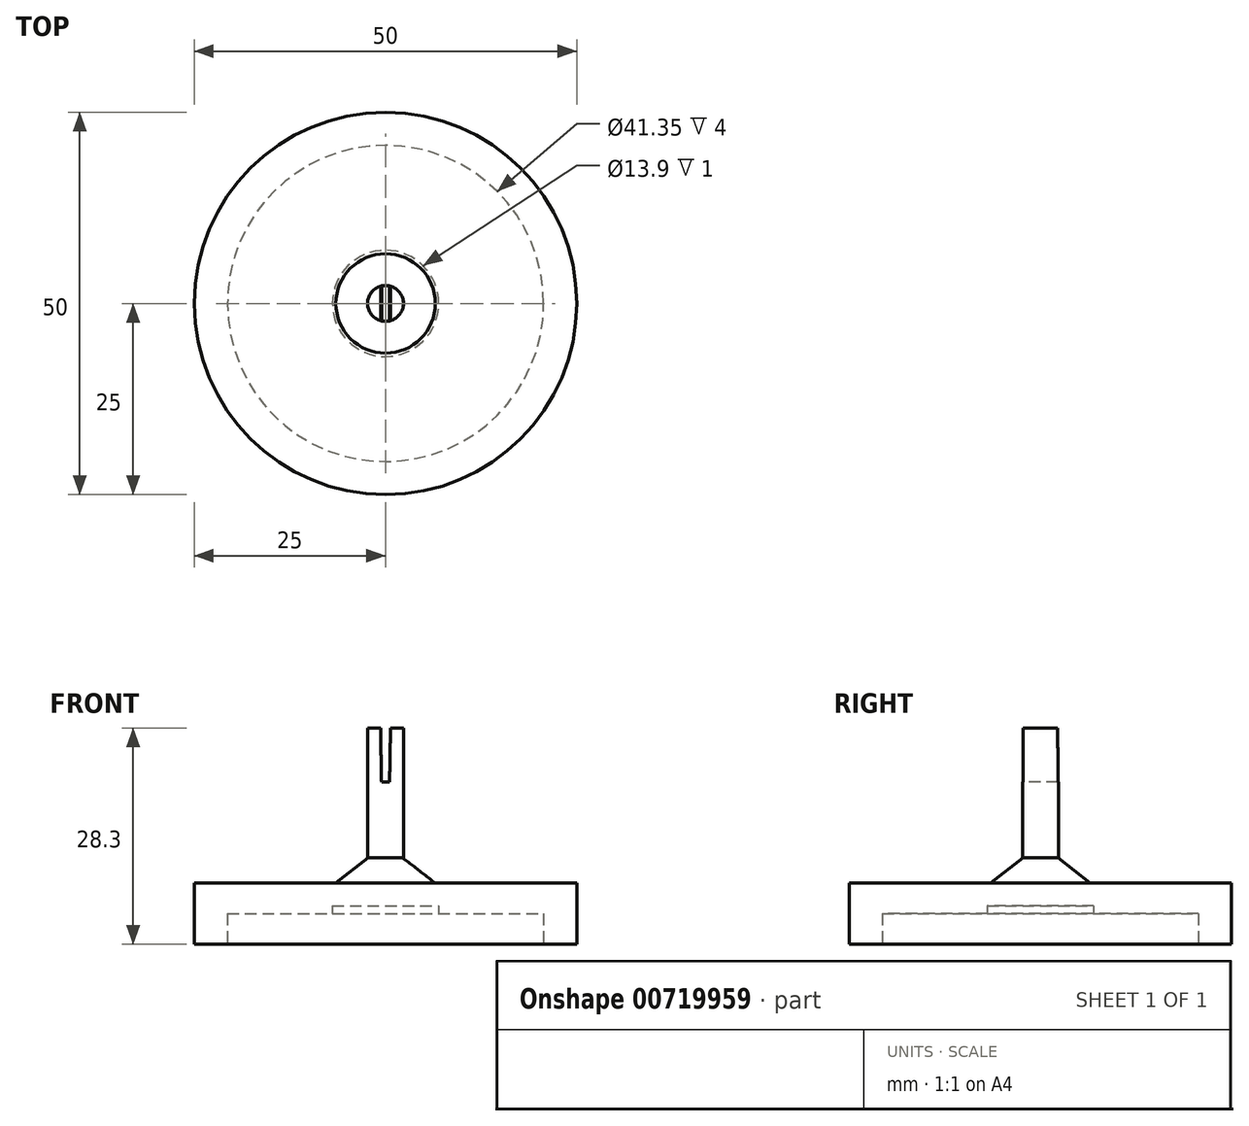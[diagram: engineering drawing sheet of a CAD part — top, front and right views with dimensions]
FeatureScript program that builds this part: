
annotation { "Feature Type Name" : "Feature", "Feature Type Description" : "" }
export const myFeature = defineFeature(function(context is Context, id is Id, definition is map)
    precondition{}
    {
        {
            var Q0;
            Q0=qCreatedBy(makeId("Top.planeOp"),FACE);
            var sketch = newSketch(context, id + "F0", { "sketchPlane" : qUnion([Q0])});
            skCircle(sketch, "E0", {"center": v(0, 0) * mm, "radius": 25 * mm});
            skSolve(sketch);
        }
        {
            var Q0;
            Q0 = qSketchRegion(id + "F0", true);
            extrude(context, id + "F1", {"entities" : qUnion([Q0]), "depth" : 8 * mm, "offsetDistance" : 25 * mm});
        }
        {
            var Q0;
            Q0=makeQuery(id+"F1.opExtrude","CAP_FACE",FACE,{"disambiguationData":[OSD([sQuery(id+"F0.wireOp",EDGE,"E0")])],"isStart":true});
            var sketch = newSketch(context, id + "F2", { "sketchPlane" : qUnion([Q0])});
            skCircle(sketch, "E1", {"center": v(0, 0) * mm, "radius": 20.68 * mm});
            skSolve(sketch);
        }
        {
            var Q0;
            Q0=makeQuery(id+"F2.imprint","IMPRINT",FACE,{"disambiguationData":[TD([[makeQuery(id+"F2.imprint","IMPRINT",EDGE,{"derivedFrom":sQuery(id+"F2.wireOp",EDGE,"E1")}),1.0]])]});
            extrude(context, id + "F3", {"entities" : qUnion([Q0]), "operationType" : NewBodyOperationType.REMOVE, "oppositeDirection" : true, "depth" : 4 * mm, "offsetDistance" : 25 * mm});
        }
        {
            var Q0;
            Q0=makeQuery(id+"F3.boolean.opBoolean","COPY",FACE,{"derivedFrom":makeQuery(id+"F3.opExtrude","CAP_FACE",FACE,{"disambiguationData":[OSD([sQuery(id+"F2.wireOp",EDGE,"E1")])],"isStart":false})});
            var sketch = newSketch(context, id + "F4", { "sketchPlane" : qUnion([Q0])});
            skCircle(sketch, "E2", {"center": v(0, 0) * mm, "radius": 6.95 * mm});
            skSolve(sketch);
        }
        {
            var Q0;
            Q0 = qSketchRegion(id + "F4", true);
            extrude(context, id + "F5", {"entities" : qUnion([Q0]), "operationType" : NewBodyOperationType.REMOVE, "oppositeDirection" : true, "depth" : 1 * mm, "offsetDistance" : 25 * mm});
        }
        {
            var Q0;
            Q0=makeQuery(id+"F1.opExtrude","CAP_FACE",FACE,{"disambiguationData":[OSD([sQuery(id+"F0.wireOp",EDGE,"E0")])],"isStart":false});
            var sketch = newSketch(context, id + "F6", { "sketchPlane" : qUnion([Q0])});
            skCircle(sketch, "E3", {"center": v(0, 0) * mm, "radius": 6.5 * mm});
            skSolve(sketch);
        }
        {
            var Q0;
            Q0=makeQuery(id+"F6.imprint","IMPRINT",FACE,{"disambiguationData":[TD([[makeQuery(id+"F6.imprint","IMPRINT",EDGE,{"derivedFrom":sQuery(id+"F6.wireOp",EDGE,"E3")}),1.0]])]});
            var Q1;
            Q1 = qSketchRegion(id + "F12", true);
            extrude(context, id + "F7", {"entities" : qUnion([Q0, Q1]), "operationType" : NewBodyOperationType.ADD, "depth" : 3.3 * mm, "offsetDistance" : 25 * mm, "hasDraft" : true, "draftAngle" : 52 * degree, "draftPullDirection" : true});
        }
        {
            var Q0;
            Q0=makeQuery(id+"F7.opExtrude","CAP_FACE",FACE,{"disambiguationData":[OSD([sQuery(id+"F6.wireOp",EDGE,"E3")])],"isStart":false});
            var sketch = newSketch(context, id + "F8", { "sketchPlane" : qUnion([Q0])});
            skCircle(sketch, "E4", {"center": v(0, 0) * mm, "radius": 2.35 * mm});
            skSolve(sketch);
        }
        {
            var Q0;
            Q0 = qSketchRegion(id + "F8", true);
            extrude(context, id + "F9", {"entities" : qUnion([Q0]), "operationType" : NewBodyOperationType.ADD, "depth" : 17 * mm, "offsetDistance" : 25 * mm});
        }
        {
            var Q0;
            Q0=makeQuery(id+"F9.opExtrude","CAP_FACE",FACE,{"disambiguationData":[OSD([sQuery(id+"F8.wireOp",EDGE,"E4")])],"isStart":false});
            var sketch = newSketch(context, id + "F10", { "sketchPlane" : qUnion([Q0])});
            skLineSegment(sketch, "E5.bottom", {"start": v(0.65, -4) * mm, "end": v(-0.65, -4) * mm});
            skLineSegment(sketch, "E5.top", {"start": v(0.65, 4) * mm, "end": v(-0.65, 4) * mm});
            skLineSegment(sketch, "E5.left", {"start": v(0.65, -4) * mm, "end": v(0.65, 4) * mm});
            skLineSegment(sketch, "E5.right", {"start": v(-0.65, -4) * mm, "end": v(-0.65, 4) * mm});
            skPoint(sketch, "E5.middle", {"position": v(0, 0) * mm});
            skSolve(sketch);
        }
        {
            var Q0;
            {var subQ0=sQuery(id+"F10.wireOp",EDGE,"E5.top");Q0=makeQuery(id+"F10.imprint","IMPRINT",FACE,{"disambiguationData":[TD([[makeQuery(id+"F10.imprint","IMPRINT",EDGE,{"derivedFrom":subQ0}),1.0]])]});}
            var Q1;
            {var subQ0=sQuery(id+"F10.wireOp",EDGE,"E5.left");var subQ1=makeQuery(id+"F9.opExtrude","CAP_EDGE",EDGE,{"disambiguationData":[OSD([sQuery(id+"F8.wireOp",EDGE,"E4")])],"isStart":false});var subQ2=makeQuery(id+"F10.imprint","INTERSECT",VERTEX,{"disambiguationData":[OD(0.0)],"derivedFrom":[subQ1,subQ0]});Q1=makeQuery(id+"F10.imprint","IMPRINT",FACE,{"disambiguationData":[TD([[makeQuery(id+"F10.imprint","IMPRINT",EDGE,{"disambiguationData":[TD([[subQ2,-1.0]])],"derivedFrom":subQ0}),1.0]])]});}
            var Q2;
            {var subQ0=sQuery(id+"F10.wireOp",EDGE,"E5.bottom");Q2=makeQuery(id+"F10.imprint","IMPRINT",FACE,{"disambiguationData":[TD([[makeQuery(id+"F10.imprint","IMPRINT",EDGE,{"derivedFrom":subQ0}),-1.0]])]});}
            extrude(context, id + "F11", {"entities" : qUnion([Q0, Q1, Q2]), "operationType" : NewBodyOperationType.REMOVE, "oppositeDirection" : true, "depth" : 7.1 * mm, "offsetDistance" : 25 * mm, "hasDraft" : true, "draftAngle" : 1 * degree, "draftPullDirection" : true});
        }
    });
